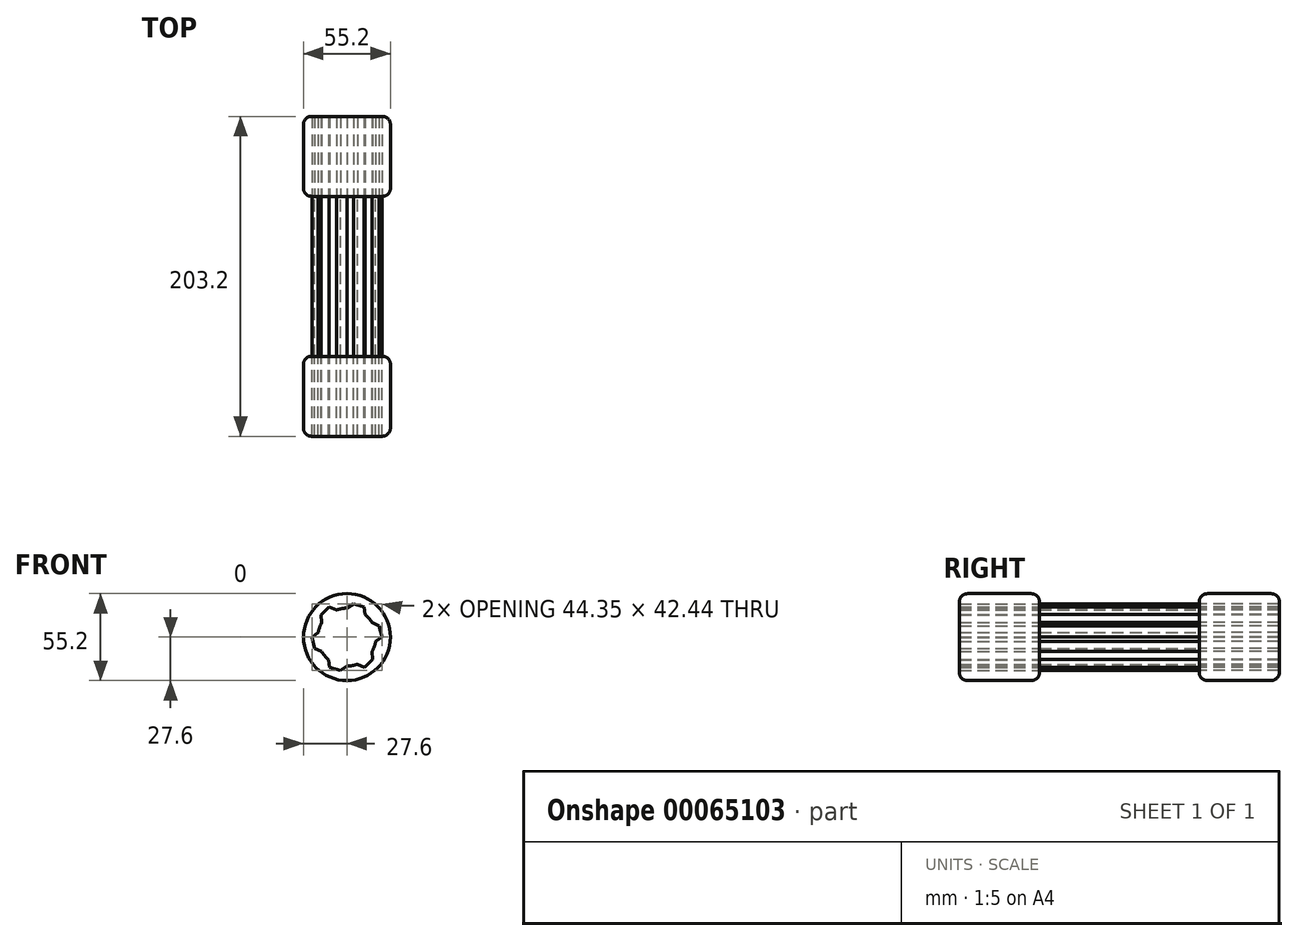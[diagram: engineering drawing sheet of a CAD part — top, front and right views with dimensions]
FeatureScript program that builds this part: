
annotation { "Feature Type Name" : "Feature", "Feature Type Description" : "" }
export const myFeature = defineFeature(function(context is Context, id is Id, definition is map)
    precondition{}
    {
        {
            var Q0;
            Q0=qCreatedBy(makeId("Front.planeOp"),FACE);
            var sketch = newSketch(context, id + "F0", { "sketchPlane" : qUnion([Q0])});
            skCircle(sketch, "E0", {"center": v(0, 0) * mm, "radius": 18.43 * mm});
            skPoint(sketch, "E1.start.orphan", {"position": v(0, 18.43) * mm});
            skLineSegment(sketch, "E2", {"start": v(0, 18.43) * mm, "end": v(4.07, 21.22) * mm});
            skLineSegment(sketch, "E3", {"start": v(4.07, 21.22) * mm, "end": v(10.87, 19.33) * mm});
            skLineSegment(sketch, "E4", {"start": v(10.87, 19.33) * mm, "end": v(11.59, 14.33) * mm});
            skLineSegment(sketch, "E5.1.0", {"start": v(-11.3, 19.08) * mm, "end": v(-6.62, 17.2) * mm});
            skLineSegment(sketch, "E5.1.1", {"start": v(-16.34, 14.13) * mm, "end": v(-11.3, 19.08) * mm});
            skLineSegment(sketch, "E5.1.2", {"start": v(-15.96, 9.22) * mm, "end": v(-16.34, 14.13) * mm});
            skLineSegment(sketch, "E5.2.0", {"start": v(-22.18, -0.25) * mm, "end": v(-18.2, 2.87) * mm});
            skLineSegment(sketch, "E5.2.1", {"start": v(-20.4, -7.09) * mm, "end": v(-22.18, -0.25) * mm});
            skLineSegment(sketch, "E5.2.2", {"start": v(-15.96, -9.22) * mm, "end": v(-20.4, -7.09) * mm});
            skLineSegment(sketch, "E5.3.0", {"start": v(-10.87, -19.33) * mm, "end": v(-11.59, -14.33) * mm});
            skLineSegment(sketch, "E5.3.1", {"start": v(-4.07, -21.22) * mm, "end": v(-10.87, -19.33) * mm});
            skLineSegment(sketch, "E5.3.2", {"start": v(0, -18.43) * mm, "end": v(-4.07, -21.22) * mm});
            skLineSegment(sketch, "E5.4.0", {"start": v(11.3, -19.08) * mm, "end": v(6.62, -17.2) * mm});
            skLineSegment(sketch, "E5.4.1", {"start": v(16.34, -14.13) * mm, "end": v(11.3, -19.08) * mm});
            skLineSegment(sketch, "E5.4.2", {"start": v(15.96, -9.22) * mm, "end": v(16.34, -14.13) * mm});
            skLineSegment(sketch, "E5.5.0", {"start": v(22.18, 0.25) * mm, "end": v(18.2, -2.87) * mm});
            skLineSegment(sketch, "E5.5.1", {"start": v(20.4, 7.09) * mm, "end": v(22.18, 0.25) * mm});
            skLineSegment(sketch, "E5.5.2", {"start": v(15.96, 9.22) * mm, "end": v(20.4, 7.09) * mm});
            skSolve(sketch);
        }
        {
            var Q0;
            Q0 = qSketchRegion(id + "F0", true);
            extrude(context, id + "F1", {"entities" : qUnion([Q0]), "depth" : 101.6 * mm});
        }
        {
            var Q0;
            Q0=makeQuery(id+"F1.opExtrude","CAP_FACE",FACE,{"disambiguationData":[OSD([sQuery(id+"F0.wireOp",EDGE,"E0"),sQuery(id+"F0.wireOp",EDGE,"E2"),sQuery(id+"F0.wireOp",EDGE,"E3"),sQuery(id+"F0.wireOp",EDGE,"E4"),sQuery(id+"F0.wireOp",EDGE,"E5.1.0"),sQuery(id+"F0.wireOp",EDGE,"E5.1.1"),sQuery(id+"F0.wireOp",EDGE,"E5.1.2"),sQuery(id+"F0.wireOp",EDGE,"E5.2.0"),sQuery(id+"F0.wireOp",EDGE,"E5.2.1"),sQuery(id+"F0.wireOp",EDGE,"E5.2.2"),sQuery(id+"F0.wireOp",EDGE,"E5.3.0"),sQuery(id+"F0.wireOp",EDGE,"E5.3.1"),sQuery(id+"F0.wireOp",EDGE,"E5.3.2"),sQuery(id+"F0.wireOp",EDGE,"E5.4.0"),sQuery(id+"F0.wireOp",EDGE,"E5.4.1"),sQuery(id+"F0.wireOp",EDGE,"E5.4.2"),sQuery(id+"F0.wireOp",EDGE,"E5.5.0"),sQuery(id+"F0.wireOp",EDGE,"E5.5.1"),sQuery(id+"F0.wireOp",EDGE,"E5.5.2")])],"isStart":true});
            var sketch = newSketch(context, id + "F2", { "sketchPlane" : qUnion([Q0])});
            skCircle(sketch, "E6", {"center": v(0, 0) * mm, "radius": 27.6 * mm});
            skSolve(sketch);
        }
        {
            var Q0;
            Q0=makeQuery(id+"F2.imprint","IMPRINT",FACE,{"disambiguationData":[TD([[makeQuery(id+"F2.imprint","IMPRINT",EDGE,{"derivedFrom":sQuery(id+"F2.wireOp",EDGE,"E6")}),1.0]])]});
            extrude(context, id + "F3", {"entities" : qUnion([Q0]), "depth" : 50.8 * mm});
        }
        {
            var Q0;
            Q0=makeQuery(id+"F3.opExtrude","SWEPT_FACE",FACE,{"disambiguationData":[OSD([sQuery(id+"F2.wireOp",EDGE,"E6")])]});
            fillet(context, id + "F4", {"entities" : qUnion([Q0]), "radius" : 5.08 * mm, "tangentPropagation" : true, "allowEdgeOverflow" : false});
        }
        {
            var Q0;
            Q0=qCreatedBy(makeId("Front.planeOp"),FACE);
            cPlane(context, id + "F5", {"entities" : qUnion([Q0]), "cplaneType" : CPlaneType.OFFSET, "offset" : 50.8 * mm, "width" : 152.4 * mm, "height" : 152.4 * mm});
        }
        {
            var Q0;
            Q0=makeQuery(id+"F3.opExtrude","SWEPT_BODY",BODY,{"disambiguationData":[OSD([sQuery(id+"F0.wireOp",EDGE,"E0"),sQuery(id+"F0.wireOp",EDGE,"E2"),sQuery(id+"F0.wireOp",EDGE,"E3"),sQuery(id+"F0.wireOp",EDGE,"E4"),sQuery(id+"F0.wireOp",EDGE,"E5.1.0"),sQuery(id+"F0.wireOp",EDGE,"E5.1.1"),sQuery(id+"F0.wireOp",EDGE,"E5.1.2"),sQuery(id+"F0.wireOp",EDGE,"E5.2.0"),sQuery(id+"F0.wireOp",EDGE,"E5.2.1"),sQuery(id+"F0.wireOp",EDGE,"E5.2.2"),sQuery(id+"F0.wireOp",EDGE,"E5.3.0"),sQuery(id+"F0.wireOp",EDGE,"E5.3.1"),sQuery(id+"F0.wireOp",EDGE,"E5.3.2"),sQuery(id+"F0.wireOp",EDGE,"E5.4.0"),sQuery(id+"F0.wireOp",EDGE,"E5.4.1"),sQuery(id+"F0.wireOp",EDGE,"E5.4.2"),sQuery(id+"F0.wireOp",EDGE,"E5.5.0"),sQuery(id+"F0.wireOp",EDGE,"E5.5.1"),sQuery(id+"F0.wireOp",EDGE,"E5.5.2"),sQuery(id+"F2.wireOp",EDGE,"E6")])]});
            var Q1;
            Q1=qCreatedBy(id+"F5.planeOp",FACE);
            mirror(context, id + "F6", {"entities" : qUnion([Q0]), "mirrorPlane" : qUnion([Q1])});
        }
    });
